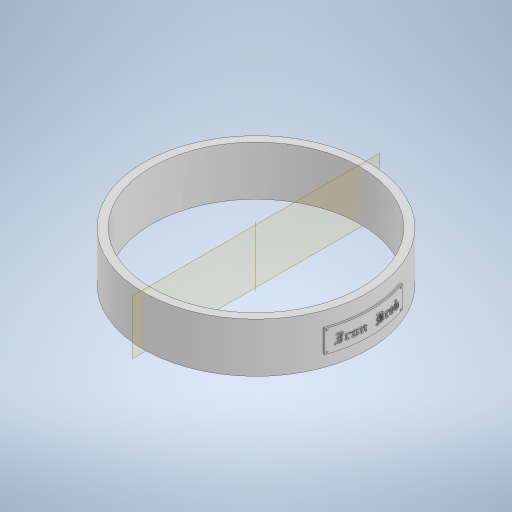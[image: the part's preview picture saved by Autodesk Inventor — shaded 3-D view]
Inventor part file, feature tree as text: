
AUTODESK INVENTOR PART (.ipt)
format: ipt  version: 2023 (Build 270158000, 158)  size: 3,224,576 bytes
history: native  units: in
note: dims shown in document units (in); Inventor stores cm internally (conversion verified against a paired STEP export)
features: emboss x3, pattern_circular x3, other x2, extrude x1, plane x1, fillet x1, sketch x1
ambient origin geometry x8: Origin, YZ Plane, XZ Plane, XY Plane, X Axis, Y Axis, Z Axis, Center Point
bodies: Solid1 (feature_tree)
feature tree (12):
  extrude  "Extrusion1"  Depth=0.3937in
  plane  "Work Plane1"
  other  "Text"
  emboss  "Emboss4"
  emboss  "Emboss5"
  emboss  "Emboss6"
  fillet  "Rivots"  Radius=0.8661in
  pattern_circular  "Circular Pattern1"  Count=6  [1 undecoded]
  pattern_circular  "Circular Pattern2"  [2 undecoded]
  pattern_circular  "Circular Pattern3"  [2 undecoded]
  sketch  "Sketch1"  dims[d0=3.937in d1=3.6614in d2=0.8661in d3=0.0in d4=2.3622in d6=0.4546in d10=0.0in d11=0.3937in d12=1.378in d19=0.0in d20=0.0in d21=0.0295in d22=0.0in d23=0.0197in d24=0.0in d25=0.0295in d26=0.0295in d27=0.0295in d28=0.0157in d29=0.0in d30=0.0138in d31=0.7874in d32=360.0deg d34=0.7874in d35=360.0deg d37=0.7874in d38=360.0deg d33=0.0in]
  other  "NamePlate"
note: 5 required parameter values undecoded (feature->parameter linkage not recoverable at this tier; creation-order binding heuristic only, values carry confidence <= 0.55)
